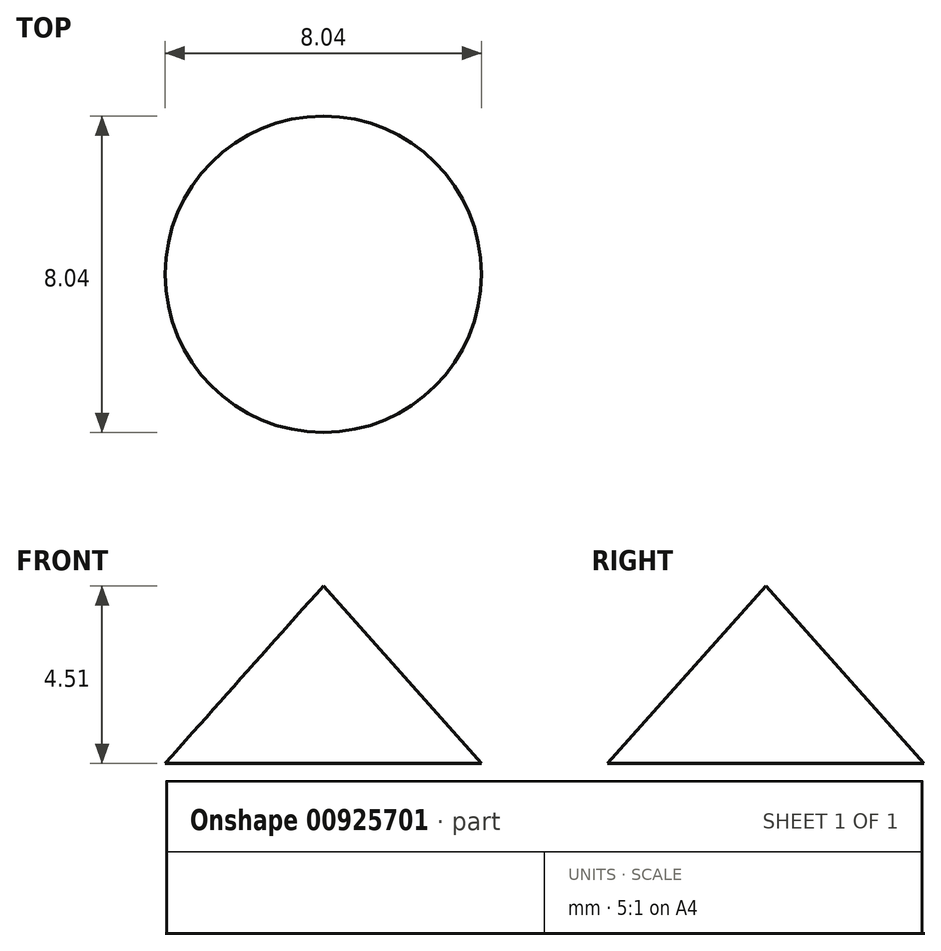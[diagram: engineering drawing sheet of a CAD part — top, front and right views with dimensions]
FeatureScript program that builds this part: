
annotation { "Feature Type Name" : "Feature", "Feature Type Description" : "" }
export const myFeature = defineFeature(function(context is Context, id is Id, definition is map)
    precondition{}
    {
        {
            var Q0;
            Q0=qCreatedBy(makeId("Front.planeOp"),FACE);
            var sketch = newSketch(context, id + "F0", { "sketchPlane" : qUnion([Q0])});
            skLineSegment(sketch, "E0", {"start": v(0, 0) * mm, "end": v(0, 4.5) * mm});
            skLineSegment(sketch, "E1", {"start": v(0, 0) * mm, "end": v(-4.02, 0) * mm});
            skLineSegment(sketch, "E2", {"start": v(0, 4.5) * mm, "end": v(-4.02, 0) * mm});
            skSolve(sketch);
        }
        {
            var Q0;
            Q0=makeQuery(id+"F0.imprint","IMPRINT",FACE,{"disambiguationData":[TD([[makeQuery(id+"F0.imprint","IMPRINT",EDGE,{"derivedFrom":sQuery(id+"F0.wireOp",EDGE,"E0")}),1.0]])]});
            var Q1;
            Q1=sQuery(id+"F0.wireOp",EDGE,"E0");
            var Q2;
            Q2=sQuery(id+"F0.wireOp",EDGE,"E0");
            revolve(context, id + "F1", {"surfaceOperationType" : NewSurfaceOperationType.NEW, "entities" : qUnion([Q0]), "surfaceEntities" : qUnion([Q1]), "axis" : qUnion([Q2]), "revolveType" : RevolveType.ONE_DIRECTION, "angle" : 360 * degree});
        }
    });
